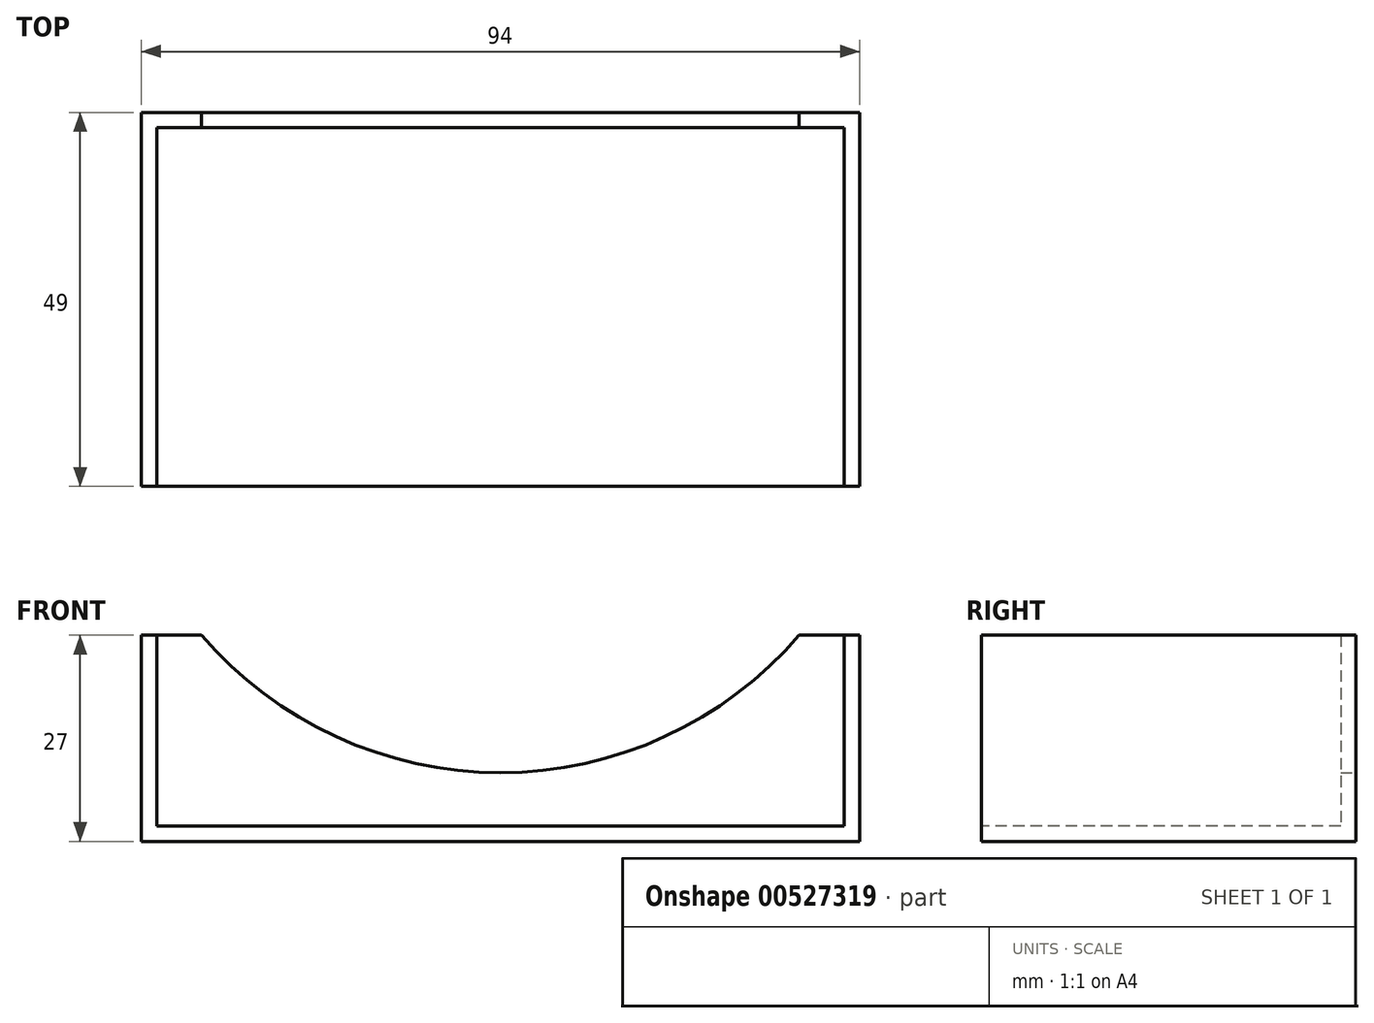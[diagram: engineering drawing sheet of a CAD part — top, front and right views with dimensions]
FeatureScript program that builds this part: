
annotation { "Feature Type Name" : "Feature", "Feature Type Description" : "" }
export const myFeature = defineFeature(function(context is Context, id is Id, definition is map)
    precondition{}
    {
        {
            var Q0;
            Q0=qCreatedBy(makeId("Top.planeOp"),FACE);
            var sketch = newSketch(context, id + "F0", { "sketchPlane" : qUnion([Q0])});
            skLineSegment(sketch, "E0.bottom", {"start": v(47, 24.5) * mm, "end": v(-47, 24.5) * mm});
            skLineSegment(sketch, "E0.top", {"start": v(47, -24.5) * mm, "end": v(-47, -24.5) * mm});
            skLineSegment(sketch, "E0.left", {"start": v(47, 24.5) * mm, "end": v(47, -24.5) * mm});
            skLineSegment(sketch, "E0.right", {"start": v(-47, 24.5) * mm, "end": v(-47, -24.5) * mm});
            skPoint(sketch, "E0.middle", {"position": v(0, 0) * mm});
            skLineSegment(sketch, "E1.bottom", {"start": v(-45, 22.5) * mm, "end": v(45, 22.5) * mm});
            skLineSegment(sketch, "E1.left", {"start": v(-45, 22.5) * mm, "end": v(-45, -22.5) * mm});
            skLineSegment(sketch, "E1.right", {"start": v(45, 22.5) * mm, "end": v(45, -22.5) * mm});
            skLineSegment(sketch, "E2", {"start": v(-45, -22.5) * mm, "end": v(-45, -24.5) * mm});
            skLineSegment(sketch, "E3", {"start": v(45, -22.5) * mm, "end": v(45, -24.5) * mm});
            skSolve(sketch);
        }
        {
            var Q0;
            Q0=makeQuery(id+"F0.imprint","IMPRINT",FACE,{"disambiguationData":[TD([[makeQuery(id+"F0.imprint","IMPRINT",EDGE,{"derivedFrom":sQuery(id+"F0.wireOp",EDGE,"E1.bottom")}),-1.0]])]});
            extrude(context, id + "F1", {"entities" : qUnion([Q0]), "depth" : 2 * mm, "offsetDistance" : 25 * mm});
        }
        {
            var Q0;
            Q0=makeQuery(id+"F0.imprint","IMPRINT",FACE,{"disambiguationData":[TD([[makeQuery(id+"F0.imprint","IMPRINT",EDGE,{"derivedFrom":sQuery(id+"F0.wireOp",EDGE,"E0.bottom")}),1.0]])]});
            extrude(context, id + "F2", {"entities" : qUnion([Q0]), "operationType" : NewBodyOperationType.ADD, "depth" : 27 * mm, "offsetDistance" : 25 * mm});
        }
        {
            var Q0;
            Q0=makeQuery(id+"F2.opExtrude","SWEPT_FACE",FACE,{"disambiguationData":[OSD([sQuery(id+"F0.wireOp",EDGE,"E0.bottom")])]});
            var sketch = newSketch(context, id + "F3", { "sketchPlane" : qUnion([Q0])});
            skCircle(sketch, "E4", {"center": v(0, 60.5) * mm, "radius": 51.5 * mm});
            skSolve(sketch);
        }
        {
            var Q0;
            {var subQ0=sQuery(id+"F3.wireOp",EDGE,"E4");var subQ1=makeQuery(id+"F2.opExtrude","CAP_EDGE",EDGE,{"disambiguationData":[OSD([sQuery(id+"F0.wireOp",EDGE,"E0.bottom")])],"isStart":false});var subQ2=makeQuery(id+"F3.imprint","INTERSECT",VERTEX,{"disambiguationData":[OD(0.0)],"derivedFrom":[subQ1,subQ0]});Q0=makeQuery(id+"F3.imprint","IMPRINT",FACE,{"disambiguationData":[TD([[makeQuery(id+"F3.imprint","IMPRINT",EDGE,{"disambiguationData":[TD([[subQ2,-1.0]])],"derivedFrom":subQ0}),1.0]])]});}
            extrude(context, id + "F4", {"entities" : qUnion([Q0]), "operationType" : NewBodyOperationType.REMOVE, "oppositeDirection" : true, "depth" : 25 * mm, "offsetDistance" : 25 * mm});
        }
    });
